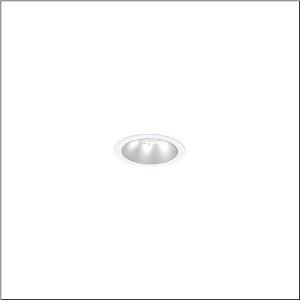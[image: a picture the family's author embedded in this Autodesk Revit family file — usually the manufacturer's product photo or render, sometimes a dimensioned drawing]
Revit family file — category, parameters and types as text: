
# Revit family: lunis_21_s_51db19ta91c
name_source: partatom
category: Lighting Fixtures
units: mm (PartAtom-declared; Revit-internal decimal feet)

## family parameters
Cut with Voids When Loaded = No
Host = Face
Light Source = No
Part Type = Normal
Room Calculation Point = No
Round Connector Dimension = Use Diameter
Shared = No

## types (1)
- --- (1 x LED 3000 K ... 6500 K, 1210 lm, 8 W, 4000K)
    Apparent Load = 8 VA
    CIE Flux Codes = 90 98 100 100 100
    Color Rendering = 80
    Color Temperature = 4000K
    Default Elevation = 1800 mm
    Description = Lunis 21,  S, downlight, light control with lens, of PMMA, anti glare with reflector, of plastic, matt, light emission: direct distribution, LED rated luminous flux: 1.200lm, light colour: 8tw, with terminal, 5-pole, mains connection: 220..240V, AC, 50..60Hz, housing, round, of diecast aluminium, traffic white (RAL 9016), diameter: 84mm, clamping range: 1..40mm, protection rating (complete): IP20, protection rating (on room side): IP54, insulation class (complete): insulation class II (safety insulation), certification: CE, impact resistance: IK03, packaging unit: 1 piece
    Height = 0 mm  [stored 0 ft]
    Lamp = 1 x LED 3000 K ... 6500 K
    Lamp Light Flux = 1210 lm
    Lamp Power = 8 W
    Lamp count = 1
    Length = 84 mm
    Luminous efficacy = 151 lm/W
    Manufacturer = Siteco
    ModVariant = No
    Model = 51DB19TA91C
    Mounting Place = Ceiling
    Mounting Type = Recessed
    Number of Poles = 1
    OnlyDefault = Yes
    Power Factor = 1
    Product Name = Lunis 21 S
    Product group = downlight
    ProductGroupID = 400
    Protection Class = Protection class II
    Protection Degree = IP 20
    RLX_Detail_Level = 1
    RLX_Emergency_Light_Flux = 0 lm
    RLX_Emergency_Type = 0
    RLX_Emergency_Type_DB = No
    RlxData = <blob elided: 8721 chars, md5=c0979191>
    Socket = socket
    Standby Power = 0 W
    System Light Flux = 1210 lm
    System Power = 8 W
    Type Comments = individual setting: CCT=4000K, colour temperature 4000K, luminous flux: 100 % | (OFF | OFF | ON | OFF) | 200 mA
    Type Image = l_1290846.jpg
    URL = http://relux.com
    VarID = @adj_019178
    Voltage = 0 V
    Weight = 0.00 kg
    Width = 0 mm  [stored 0 ft]

note: [stored X ft] marks values corroborated as IEEE doubles in the binary element streams (Revit-internal decimal feet)

## geometry (parser evidence)
native form markers: Sweep x8
no freeform markers — native parametric forms only
